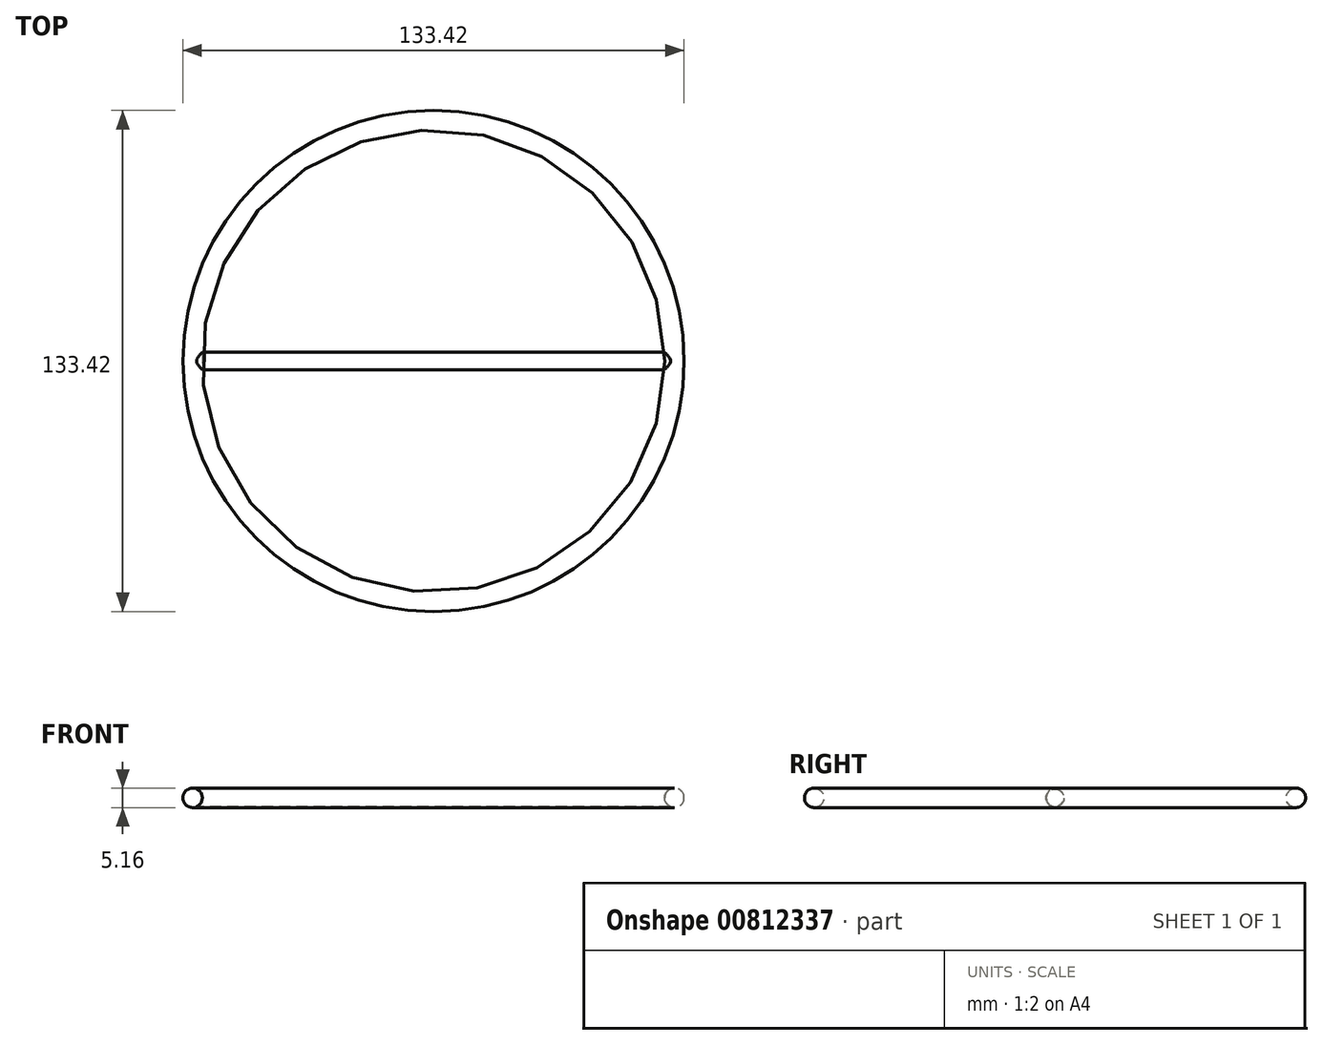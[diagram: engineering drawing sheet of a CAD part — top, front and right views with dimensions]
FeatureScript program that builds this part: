
annotation { "Feature Type Name" : "Feature", "Feature Type Description" : "" }
export const myFeature = defineFeature(function(context is Context, id is Id, definition is map)
    precondition{}
    {
        {
            var Q0;
            Q0=qCreatedBy(makeId("Front.planeOp"),FACE);
            var sketch = newSketch(context, id + "F0", { "sketchPlane" : qUnion([Q0])});
            skLineSegment(sketch, "E0", {"start": v(0, 0) * mm, "end": v(-64.12, 0) * mm});
            skCircle(sketch, "E1", {"center": v(-64.12, 0) * mm, "radius": 2.58 * mm});
            skSolve(sketch);
        }
        {
            var Q0;
            Q0=qCreatedBy(makeId("Right.planeOp"),FACE);
            var sketch = newSketch(context, id + "F1", { "sketchPlane" : qUnion([Q0])});
            skLineSegment(sketch, "E2", {"start": v(0, 23.3) * mm, "end": v(0, -21.77) * mm});
            skSolve(sketch);
        }
        {
            var Q0;
            Q0 = qSketchRegion(id + "F0", true);
            var Q1;
            Q1=sQuery(id+"F1.wireOp",EDGE,"E2");
            revolve(context, id + "F2", {"surfaceOperationType" : NewSurfaceOperationType.NEW, "entities" : qUnion([Q0]), "axis" : qUnion([Q1]), "revolveType" : RevolveType.FULL});
        }
        {
            var Q0;
            Q0=qCreatedBy(makeId("Right.planeOp"),FACE);
            var sketch = newSketch(context, id + "F3", { "sketchPlane" : qUnion([Q0])});
            skCircle(sketch, "E3", {"center": v(0, 0) * mm, "radius": 2.37 * mm});
            skSolve(sketch);
        }
        {
            var Q0;
            Q0=makeQuery(id+"F3.imprint","IMPRINT",FACE,{"disambiguationData":[TD([[makeQuery(id+"F3.imprint","IMPRINT",EDGE,{"derivedFrom":sQuery(id+"F3.wireOp",EDGE,"E3")}),1.0]])]});
            var Q1;
            Q1=makeQuery(id+"F2.opRevolve","SWEPT_FACE",FACE,{"disambiguationData":[OSD([sQuery(id+"F0.wireOp",EDGE,"E1")])]});
            var Q2;
            Q2=makeQuery(id+"F2.opRevolve","SWEPT_FACE",FACE,{"disambiguationData":[OSD([sQuery(id+"F0.wireOp",EDGE,"E1")])]});
            extrude(context, id + "F4", {"entities" : qUnion([Q0]), "endBound" : BoundingType.UP_TO_SURFACE, "depth" : 25 * mm, "endBoundEntityFace" : qUnion([Q1]), "offsetDistance" : 25 * mm, "hasSecondDirection" : true, "secondDirectionBound" : SecondDirectionBoundingType.UP_TO_SURFACE, "secondDirectionOppositeDirection" : true, "secondDirectionDepth" : 25 * mm, "secondDirectionBoundEntityFace" : qUnion([Q2])});
        }
    });
